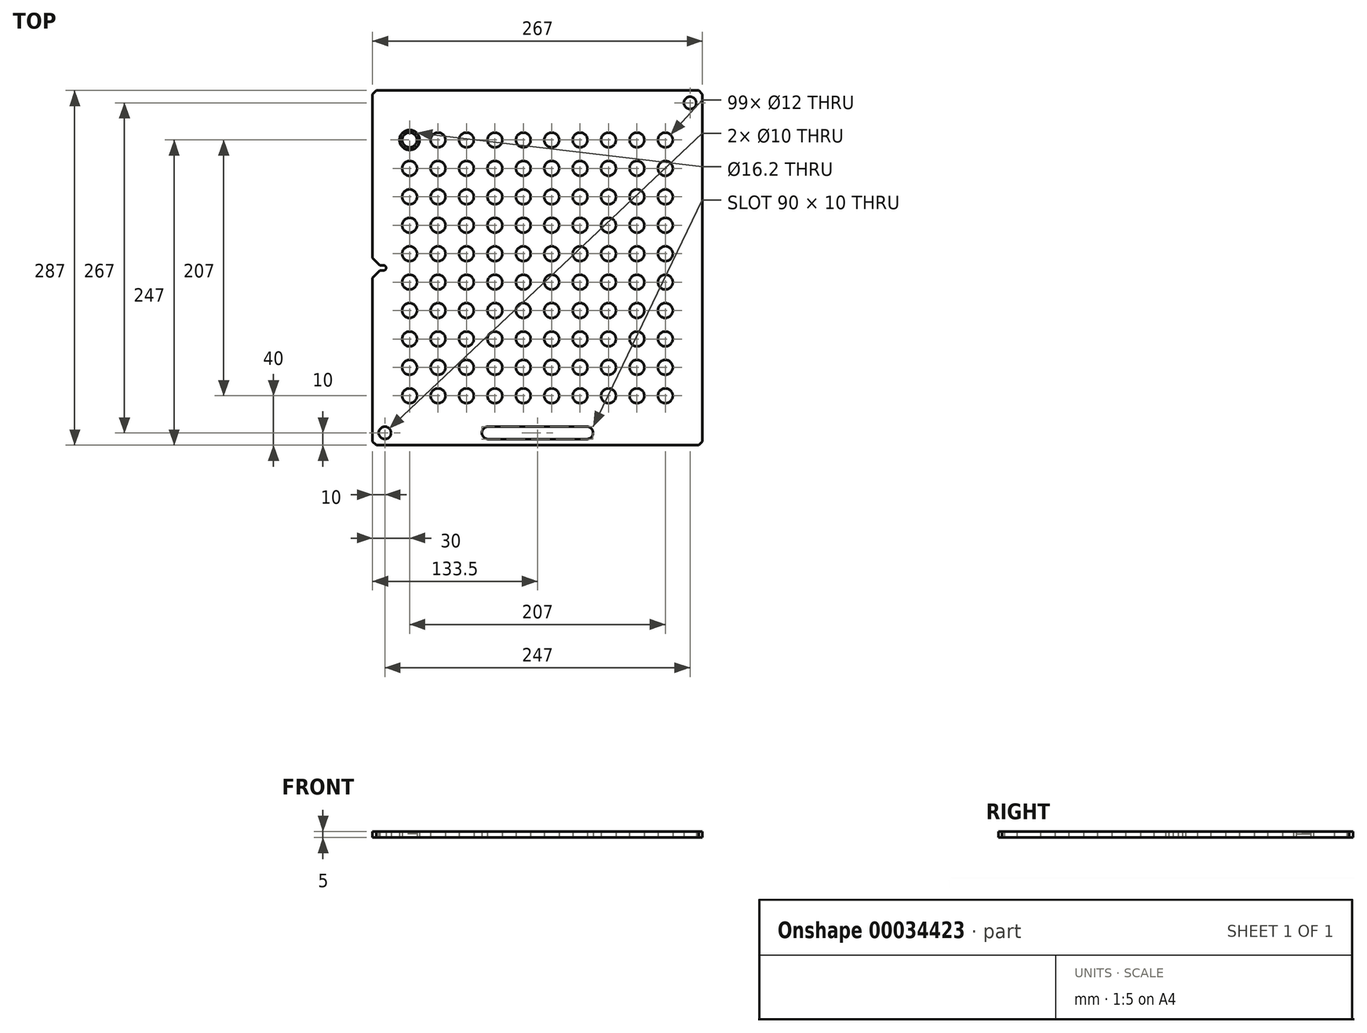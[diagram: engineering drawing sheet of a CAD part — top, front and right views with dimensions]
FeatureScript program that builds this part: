
annotation { "Feature Type Name" : "Feature", "Feature Type Description" : "" }
export const myFeature = defineFeature(function(context is Context, id is Id, definition is map)
    precondition{}
    {
        {
            var Q0;
            Q0=qCreatedBy(makeId("Top.planeOp"),FACE);
            var sketch = newSketch(context, id + "F0", { "sketchPlane" : qUnion([Q0])});
            skLineSegment(sketch, "E0", {"start": v(130.5, 143.5) * mm, "end": v(-130.5, 143.5) * mm});
            skLineSegment(sketch, "E1", {"start": v(-133.5, 140.5) * mm, "end": v(-133.5, 8) * mm});
            skLineSegment(sketch, "E2", {"start": v(130.5, -143.5) * mm, "end": v(-130.5, -143.5) * mm});
            skLineSegment(sketch, "E3", {"start": v(-133.5, 8) * mm, "end": v(-127.5, 2) * mm});
            skLineSegment(sketch, "E4", {"start": v(-124.5, 2) * mm, "end": v(-127.5, 2) * mm});
            skLineSegment(sketch, "E5", {"start": v(-124.5, -2) * mm, "end": v(-127.5, -2) * mm});
            skLineSegment(sketch, "E6", {"start": v(-133.5, -8) * mm, "end": v(-127.5, -2) * mm});
            skCircle(sketch, "E7", {"center": v(-103.5, 103.5) * mm, "radius": 6 * mm});
            skLineSegment(sketch, "E8", {"start": v(-133.5, -8) * mm, "end": v(-133.5, -140.5) * mm});
            skLineSegment(sketch, "E9", {"start": v(133.5, -140.5) * mm, "end": v(133.5, 140.5) * mm});
            skLineSegment(sketch, "E10", {"start": v(-40, -138.5) * mm, "end": v(40, -138.5) * mm});
            skLineSegment(sketch, "E11", {"start": v(-40, -128.5) * mm, "end": v(40, -128.5) * mm});
            skArc(sketch, "E12", {"start": v(40, -138.5) * mm, "mid": v(45, -133.5) * mm, "end": v(40, -128.5) * mm});
            skArc(sketch, "E13", {"start": v(-40, -128.5) * mm, "mid": v(-45, -133.5) * mm, "end": v(-40, -138.5) * mm});
            skCircle(sketch, "E14", {"center": v(123.5, 133.5) * mm, "radius": 5 * mm});
            skCircle(sketch, "E15", {"center": v(-123.5, -133.5) * mm, "radius": 5 * mm});
            skLineSegment(sketch, "E16", {"start": v(-133.5, 140.5) * mm, "end": v(-130.5, 143.5) * mm});
            skLineSegment(sketch, "E17", {"start": v(130.5, 143.5) * mm, "end": v(133.5, 140.5) * mm});
            skLineSegment(sketch, "E18", {"start": v(133.5, -140.5) * mm, "end": v(130.5, -143.5) * mm});
            skLineSegment(sketch, "E19", {"start": v(-130.5, -143.5) * mm, "end": v(-133.5, -140.5) * mm});
            skCircle(sketch, "E20", {"center": v(-103.5, 103.5) * mm, "radius": 8.1 * mm});
            skArc(sketch, "E21", {"start": v(-124.5, -2) * mm, "mid": v(-122.5, 0) * mm, "end": v(-124.5, 2) * mm});
            skCircle(sketch, "E22.0.1.0", {"center": v(-103.5, 80.5) * mm, "radius": 6 * mm});
            skCircle(sketch, "E22.0.2.0", {"center": v(-103.5, 57.5) * mm, "radius": 6 * mm});
            skCircle(sketch, "E22.0.3.0", {"center": v(-103.5, 34.5) * mm, "radius": 6 * mm});
            skCircle(sketch, "E22.0.4.0", {"center": v(-103.5, 11.5) * mm, "radius": 6 * mm});
            skCircle(sketch, "E22.0.5.0", {"center": v(-103.5, -11.5) * mm, "radius": 6 * mm});
            skCircle(sketch, "E22.0.6.0", {"center": v(-103.5, -34.5) * mm, "radius": 6 * mm});
            skCircle(sketch, "E22.0.7.0", {"center": v(-103.5, -57.5) * mm, "radius": 6 * mm});
            skCircle(sketch, "E22.0.8.0", {"center": v(-103.5, -80.5) * mm, "radius": 6 * mm});
            skCircle(sketch, "E22.0.9.0", {"center": v(-103.5, -103.5) * mm, "radius": 6 * mm});
            skCircle(sketch, "E22.1.0.0", {"center": v(-80.5, 103.5) * mm, "radius": 6 * mm});
            skCircle(sketch, "E22.1.1.0", {"center": v(-80.5, 80.5) * mm, "radius": 6 * mm});
            skCircle(sketch, "E22.1.2.0", {"center": v(-80.5, 57.5) * mm, "radius": 6 * mm});
            skCircle(sketch, "E22.1.3.0", {"center": v(-80.5, 34.5) * mm, "radius": 6 * mm});
            skCircle(sketch, "E22.1.4.0", {"center": v(-80.5, 11.5) * mm, "radius": 6 * mm});
            skCircle(sketch, "E22.1.5.0", {"center": v(-80.5, -11.5) * mm, "radius": 6 * mm});
            skCircle(sketch, "E22.1.6.0", {"center": v(-80.5, -34.5) * mm, "radius": 6 * mm});
            skCircle(sketch, "E22.1.7.0", {"center": v(-80.5, -57.5) * mm, "radius": 6 * mm});
            skCircle(sketch, "E22.1.8.0", {"center": v(-80.5, -80.5) * mm, "radius": 6 * mm});
            skCircle(sketch, "E22.1.9.0", {"center": v(-80.5, -103.5) * mm, "radius": 6 * mm});
            skCircle(sketch, "E22.2.0.0", {"center": v(-57.5, 103.5) * mm, "radius": 6 * mm});
            skCircle(sketch, "E22.2.1.0", {"center": v(-57.5, 80.5) * mm, "radius": 6 * mm});
            skCircle(sketch, "E22.2.2.0", {"center": v(-57.5, 57.5) * mm, "radius": 6 * mm});
            skCircle(sketch, "E22.2.3.0", {"center": v(-57.5, 34.5) * mm, "radius": 6 * mm});
            skCircle(sketch, "E22.2.4.0", {"center": v(-57.5, 11.5) * mm, "radius": 6 * mm});
            skCircle(sketch, "E22.2.5.0", {"center": v(-57.5, -11.5) * mm, "radius": 6 * mm});
            skCircle(sketch, "E22.2.6.0", {"center": v(-57.5, -34.5) * mm, "radius": 6 * mm});
            skCircle(sketch, "E22.2.7.0", {"center": v(-57.5, -57.5) * mm, "radius": 6 * mm});
            skCircle(sketch, "E22.2.8.0", {"center": v(-57.5, -80.5) * mm, "radius": 6 * mm});
            skCircle(sketch, "E22.2.9.0", {"center": v(-57.5, -103.5) * mm, "radius": 6 * mm});
            skCircle(sketch, "E22.3.0.0", {"center": v(-34.5, 103.5) * mm, "radius": 6 * mm});
            skCircle(sketch, "E22.3.1.0", {"center": v(-34.5, 80.5) * mm, "radius": 6 * mm});
            skCircle(sketch, "E22.3.2.0", {"center": v(-34.5, 57.5) * mm, "radius": 6 * mm});
            skCircle(sketch, "E22.3.3.0", {"center": v(-34.5, 34.5) * mm, "radius": 6 * mm});
            skCircle(sketch, "E22.3.4.0", {"center": v(-34.5, 11.5) * mm, "radius": 6 * mm});
            skCircle(sketch, "E22.3.5.0", {"center": v(-34.5, -11.5) * mm, "radius": 6 * mm});
            skCircle(sketch, "E22.3.6.0", {"center": v(-34.5, -34.5) * mm, "radius": 6 * mm});
            skCircle(sketch, "E22.3.7.0", {"center": v(-34.5, -57.5) * mm, "radius": 6 * mm});
            skCircle(sketch, "E22.3.8.0", {"center": v(-34.5, -80.5) * mm, "radius": 6 * mm});
            skCircle(sketch, "E22.3.9.0", {"center": v(-34.5, -103.5) * mm, "radius": 6 * mm});
            skCircle(sketch, "E22.4.0.0", {"center": v(-11.5, 103.5) * mm, "radius": 6 * mm});
            skCircle(sketch, "E22.4.1.0", {"center": v(-11.5, 80.5) * mm, "radius": 6 * mm});
            skCircle(sketch, "E22.4.2.0", {"center": v(-11.5, 57.5) * mm, "radius": 6 * mm});
            skCircle(sketch, "E22.4.3.0", {"center": v(-11.5, 34.5) * mm, "radius": 6 * mm});
            skCircle(sketch, "E22.4.4.0", {"center": v(-11.5, 11.5) * mm, "radius": 6 * mm});
            skCircle(sketch, "E22.4.5.0", {"center": v(-11.5, -11.5) * mm, "radius": 6 * mm});
            skCircle(sketch, "E22.4.6.0", {"center": v(-11.5, -34.5) * mm, "radius": 6 * mm});
            skCircle(sketch, "E22.4.7.0", {"center": v(-11.5, -57.5) * mm, "radius": 6 * mm});
            skCircle(sketch, "E22.4.8.0", {"center": v(-11.5, -80.5) * mm, "radius": 6 * mm});
            skCircle(sketch, "E22.4.9.0", {"center": v(-11.5, -103.5) * mm, "radius": 6 * mm});
            skCircle(sketch, "E22.5.0.0", {"center": v(11.5, 103.5) * mm, "radius": 6 * mm});
            skCircle(sketch, "E22.5.1.0", {"center": v(11.5, 80.5) * mm, "radius": 6 * mm});
            skCircle(sketch, "E22.5.2.0", {"center": v(11.5, 57.5) * mm, "radius": 6 * mm});
            skCircle(sketch, "E22.5.3.0", {"center": v(11.5, 34.5) * mm, "radius": 6 * mm});
            skCircle(sketch, "E22.5.4.0", {"center": v(11.5, 11.5) * mm, "radius": 6 * mm});
            skCircle(sketch, "E22.5.5.0", {"center": v(11.5, -11.5) * mm, "radius": 6 * mm});
            skCircle(sketch, "E22.5.6.0", {"center": v(11.5, -34.5) * mm, "radius": 6 * mm});
            skCircle(sketch, "E22.5.7.0", {"center": v(11.5, -57.5) * mm, "radius": 6 * mm});
            skCircle(sketch, "E22.5.8.0", {"center": v(11.5, -80.5) * mm, "radius": 6 * mm});
            skCircle(sketch, "E22.5.9.0", {"center": v(11.5, -103.5) * mm, "radius": 6 * mm});
            skCircle(sketch, "E22.6.0.0", {"center": v(34.5, 103.5) * mm, "radius": 6 * mm});
            skCircle(sketch, "E22.6.1.0", {"center": v(34.5, 80.5) * mm, "radius": 6 * mm});
            skCircle(sketch, "E22.6.2.0", {"center": v(34.5, 57.5) * mm, "radius": 6 * mm});
            skCircle(sketch, "E22.6.3.0", {"center": v(34.5, 34.5) * mm, "radius": 6 * mm});
            skCircle(sketch, "E22.6.4.0", {"center": v(34.5, 11.5) * mm, "radius": 6 * mm});
            skCircle(sketch, "E22.6.5.0", {"center": v(34.5, -11.5) * mm, "radius": 6 * mm});
            skCircle(sketch, "E22.6.6.0", {"center": v(34.5, -34.5) * mm, "radius": 6 * mm});
            skCircle(sketch, "E22.6.7.0", {"center": v(34.5, -57.5) * mm, "radius": 6 * mm});
            skCircle(sketch, "E22.6.8.0", {"center": v(34.5, -80.5) * mm, "radius": 6 * mm});
            skCircle(sketch, "E22.6.9.0", {"center": v(34.5, -103.5) * mm, "radius": 6 * mm});
            skCircle(sketch, "E22.7.0.0", {"center": v(57.5, 103.5) * mm, "radius": 6 * mm});
            skCircle(sketch, "E22.7.1.0", {"center": v(57.5, 80.5) * mm, "radius": 6 * mm});
            skCircle(sketch, "E22.7.2.0", {"center": v(57.5, 57.5) * mm, "radius": 6 * mm});
            skCircle(sketch, "E22.7.3.0", {"center": v(57.5, 34.5) * mm, "radius": 6 * mm});
            skCircle(sketch, "E22.7.4.0", {"center": v(57.5, 11.5) * mm, "radius": 6 * mm});
            skCircle(sketch, "E22.7.5.0", {"center": v(57.5, -11.5) * mm, "radius": 6 * mm});
            skCircle(sketch, "E22.7.6.0", {"center": v(57.5, -34.5) * mm, "radius": 6 * mm});
            skCircle(sketch, "E22.7.7.0", {"center": v(57.5, -57.5) * mm, "radius": 6 * mm});
            skCircle(sketch, "E22.7.8.0", {"center": v(57.5, -80.5) * mm, "radius": 6 * mm});
            skCircle(sketch, "E22.7.9.0", {"center": v(57.5, -103.5) * mm, "radius": 6 * mm});
            skCircle(sketch, "E22.8.0.0", {"center": v(80.5, 103.5) * mm, "radius": 6 * mm});
            skCircle(sketch, "E22.8.1.0", {"center": v(80.5, 80.5) * mm, "radius": 6 * mm});
            skCircle(sketch, "E22.8.2.0", {"center": v(80.5, 57.5) * mm, "radius": 6 * mm});
            skCircle(sketch, "E22.8.3.0", {"center": v(80.5, 34.5) * mm, "radius": 6 * mm});
            skCircle(sketch, "E22.8.4.0", {"center": v(80.5, 11.5) * mm, "radius": 6 * mm});
            skCircle(sketch, "E22.8.5.0", {"center": v(80.5, -11.5) * mm, "radius": 6 * mm});
            skCircle(sketch, "E22.8.6.0", {"center": v(80.5, -34.5) * mm, "radius": 6 * mm});
            skCircle(sketch, "E22.8.7.0", {"center": v(80.5, -57.5) * mm, "radius": 6 * mm});
            skCircle(sketch, "E22.8.8.0", {"center": v(80.5, -80.5) * mm, "radius": 6 * mm});
            skCircle(sketch, "E22.8.9.0", {"center": v(80.5, -103.5) * mm, "radius": 6 * mm});
            skCircle(sketch, "E22.9.0.0", {"center": v(103.5, 103.5) * mm, "radius": 6 * mm});
            skCircle(sketch, "E22.9.1.0", {"center": v(103.5, 80.5) * mm, "radius": 6 * mm});
            skCircle(sketch, "E22.9.2.0", {"center": v(103.5, 57.5) * mm, "radius": 6 * mm});
            skCircle(sketch, "E22.9.3.0", {"center": v(103.5, 34.5) * mm, "radius": 6 * mm});
            skCircle(sketch, "E22.9.4.0", {"center": v(103.5, 11.5) * mm, "radius": 6 * mm});
            skCircle(sketch, "E22.9.5.0", {"center": v(103.5, -11.5) * mm, "radius": 6 * mm});
            skCircle(sketch, "E22.9.6.0", {"center": v(103.5, -34.5) * mm, "radius": 6 * mm});
            skCircle(sketch, "E22.9.7.0", {"center": v(103.5, -57.5) * mm, "radius": 6 * mm});
            skCircle(sketch, "E22.9.8.0", {"center": v(103.5, -80.5) * mm, "radius": 6 * mm});
            skCircle(sketch, "E22.9.9.0", {"center": v(103.5, -103.5) * mm, "radius": 6 * mm});
            skLineSegment(sketch, "E22.direction1", {"start": v(-103.5, 103.5) * mm, "end": v(-80.5, 103.5) * mm, "construction": true});
            skLineSegment(sketch, "E22.direction2", {"start": v(-103.5, 103.5) * mm, "end": v(-103.5, 80.5) * mm, "construction": true});
            skSolve(sketch);
        }
        {
            var Q0;
            Q0 = qSketchRegion(id + "F0", true);
            extrude(context, id + "F1", {"entities" : qUnion([Q0]), "depth" : 5 * mm});
        }
        {
            var Q0;
            Q0=makeQuery(id+"F0.imprint","IMPRINT",FACE,{"disambiguationData":[TD([[makeQuery(id+"F0.imprint","IMPRINT",EDGE,{"derivedFrom":sQuery(id+"F0.wireOp",EDGE,"E7")}),1.0]])]});
            extrude(context, id + "F2", {"entities" : qUnion([Q0]), "operationType" : NewBodyOperationType.ADD, "depth" : 3 * mm});
        }
    });
